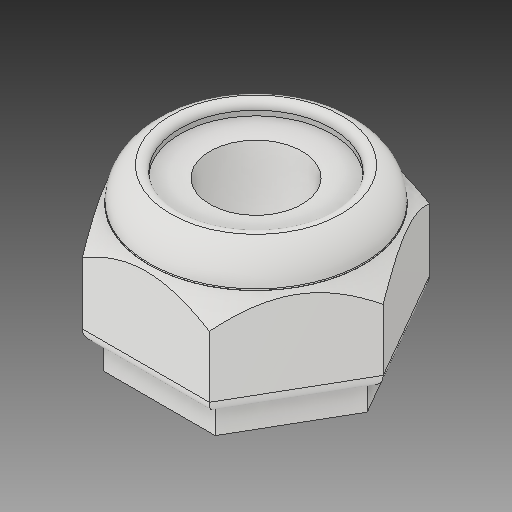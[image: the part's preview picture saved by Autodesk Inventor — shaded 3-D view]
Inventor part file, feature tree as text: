
AUTODESK INVENTOR PART (.ipt)
format: ipt  version: 2019 (Build 230136000, 136)  size: 177,152 bytes
history: native  units: in
note: dims shown in document units (in); Inventor stores cm internally (conversion verified against a paired STEP export)
features: extrude x1
ambient origin geometry x8: Origin, YZ Plane, XZ Plane, XY Plane, X Axis, Y Axis, Z Axis, Center Point
bodies: Solid1 (feature_tree)
feature tree (1):
  extrude  "Extrude1"  [1 undecoded]
note: 1 required parameter value undecoded (feature->parameter linkage not recoverable at this tier; creation-order binding heuristic only, values carry confidence <= 0.55)
